# Revit family: FantiniCosmi_BIM_7A1-1R306-00A
name_source: partatom
category: Generic Models
units: mm (PartAtom-declared; Revit-internal decimal feet)

## family parameters
Always vertical = Yes
Can host rebar = No
Cut with Voids When Loaded = No
Part Type = Normal
Room Calculation Point = No
Round Connector Dimension = Use Diameter
Shared = No
Work Plane-Based = No

## types (1)
- Standard
    Adjustment range = 0 ÷ 90 °C
    Base material = galvanized steel
    Catalog web link = https://www.fantinicosmi.it
    Compliance with = CE standard 0497 (PED)
    Default Elevation = 0 mm  [stored 0 ft]
    Description = Contact control thermostat
    Designer = Carniti
    Differential at 0 ÷ 60 ° C = 8 ± 2 ° C
    Differential at 0 ÷ 90 °  = 10 ± 2 ° C
    Max Temp. Tolerance = ± 6 ° C
    Part Number = 7A1-1R306-00A
    Rack QTY = 10
    Thermal gradient = 1 ° C / min
    Type of action = 1B
    Type of adjustment = external
    Type of sensor = bimetallic
    min Temp. Tolerance = ± 4 ° C

note: [stored X ft] marks values corroborated as IEEE doubles in the binary element streams (Revit-internal decimal feet)

## geometry (parser evidence)
native form markers: Sweep x3
no freeform markers — native parametric forms only
